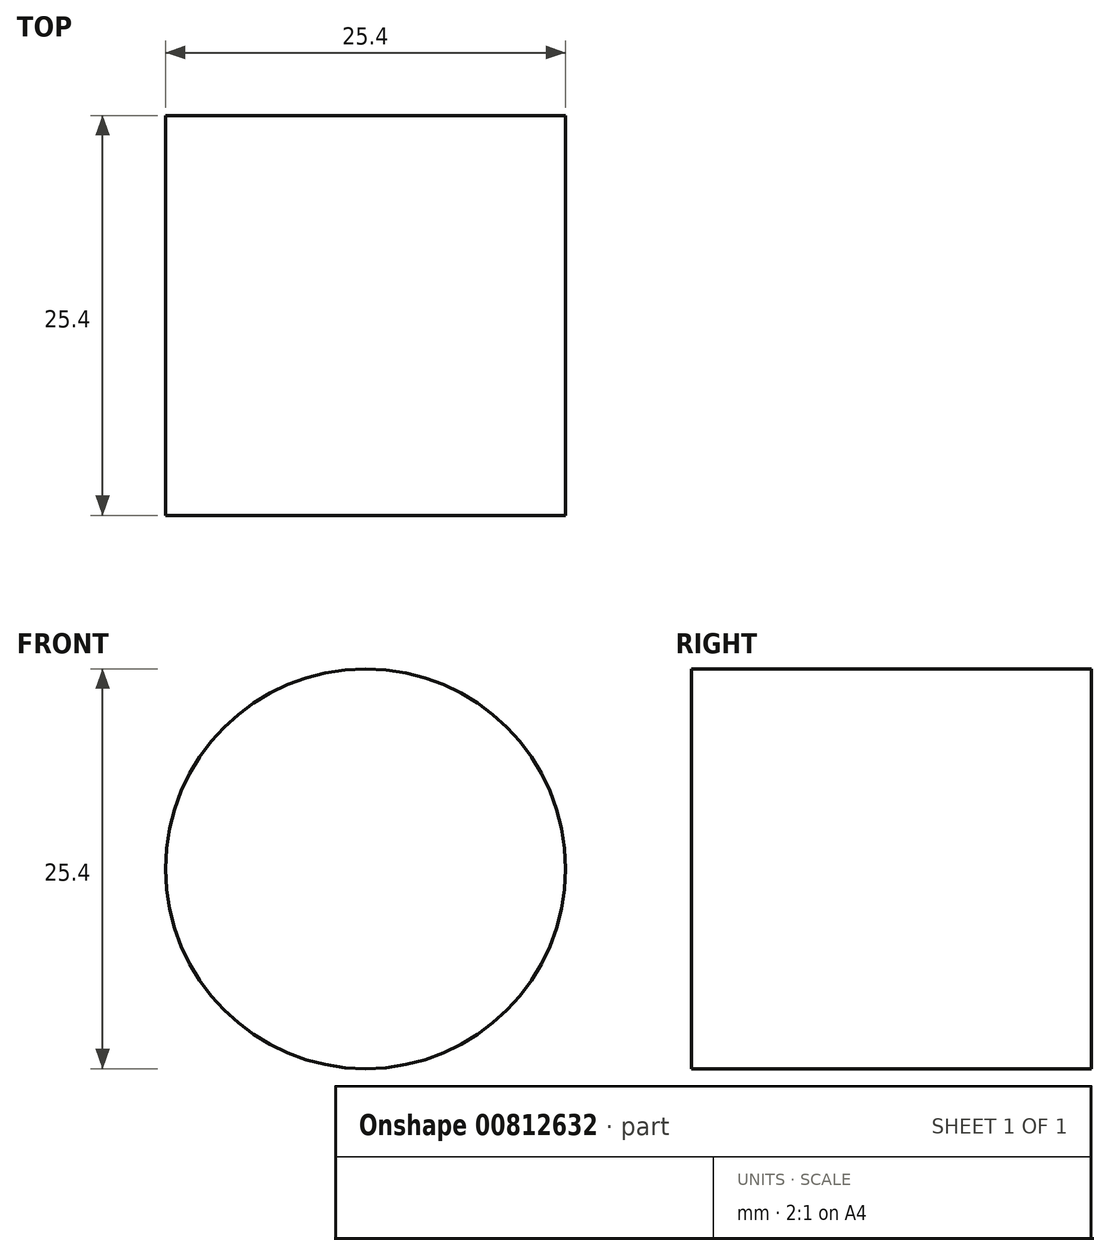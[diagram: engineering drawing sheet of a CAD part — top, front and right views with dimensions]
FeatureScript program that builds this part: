
annotation { "Feature Type Name" : "Feature", "Feature Type Description" : "" }
export const myFeature = defineFeature(function(context is Context, id is Id, definition is map)
    precondition{}
    {
        {
            var Q0;
            Q0=qCreatedBy(makeId("Front.planeOp"),FACE);
            var sketch = newSketch(context, id + "F0", { "sketchPlane" : qUnion([Q0])});
            skCircle(sketch, "E0", {"center": v(0, 0) * mm, "radius": 12.7 * mm});
            skSolve(sketch);
        }
        {
            var Q0;
            Q0=qSketchRegion(id+"F0",true);
            extrude(context, id + "F1", {"entities" : qUnion([Q0]), "depth" : 25.4 * mm, "offsetDistance" : 25.4 * mm});
        }
    });
